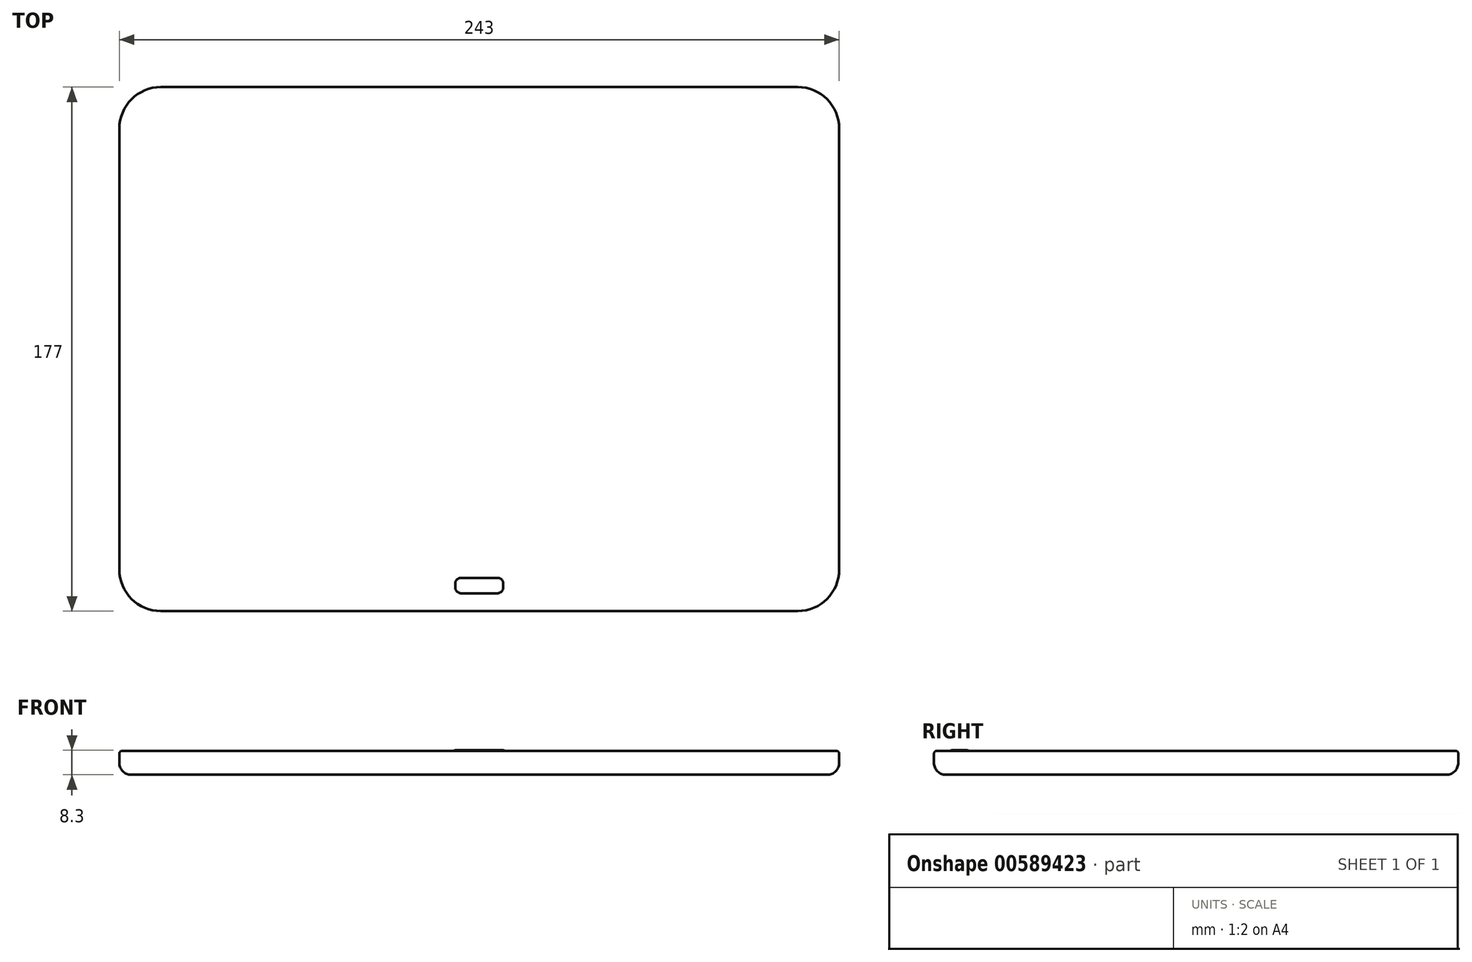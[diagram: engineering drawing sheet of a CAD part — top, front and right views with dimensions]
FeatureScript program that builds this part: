
annotation { "Feature Type Name" : "Feature", "Feature Type Description" : "" }
export const myFeature = defineFeature(function(context is Context, id is Id, definition is map)
    precondition{}
    {
        {
            var Q0;
            Q0=qCreatedBy(makeId("Top.planeOp"),FACE);
            var sketch = newSketch(context, id + "F0", { "sketchPlane" : qUnion([Q0])});
            skLineSegment(sketch, "E0.bottom", {"start": v(-121.5, 177) * mm, "end": v(121.5, 177) * mm});
            skLineSegment(sketch, "E0.top", {"start": v(-121.5, 0) * mm, "end": v(121.5, 0) * mm});
            skLineSegment(sketch, "E0.left", {"start": v(-121.5, 177) * mm, "end": v(-121.5, 0) * mm});
            skLineSegment(sketch, "E0.right", {"start": v(121.5, 177) * mm, "end": v(121.5, 0) * mm});
            skSolve(sketch);
        }
        {
            var Q0;
            Q0=makeQuery(id+"F0.imprint","IMPRINT",FACE,{"disambiguationData":[TD([[makeQuery(id+"F0.imprint","IMPRINT",EDGE,{"derivedFrom":sQuery(id+"F0.wireOp",EDGE,"E0.bottom")}),-1.0]])]});
            extrude(context, id + "F1", {"entities" : qUnion([Q0]), "depth" : 8.1 * mm, "offsetDistance" : 25 * mm});
        }
        {
            var Q0;
            Q0=makeQuery(id+"F1.opExtrude","SWEPT_EDGE",EDGE,{"disambiguationData":[OSD([sQuery(id+"F0.wireOp",EDGE,"E0.top"),sQuery(id+"F0.wireOp",EDGE,"E0.left")])]});
            var Q1;
            Q1=makeQuery(id+"F1.opExtrude","SWEPT_EDGE",EDGE,{"disambiguationData":[OSD([sQuery(id+"F0.wireOp",EDGE,"E0.top"),sQuery(id+"F0.wireOp",EDGE,"E0.right")])]});
            var Q2;
            Q2=makeQuery(id+"F1.opExtrude","SWEPT_EDGE",EDGE,{"disambiguationData":[OSD([sQuery(id+"F0.wireOp",EDGE,"E0.bottom"),sQuery(id+"F0.wireOp",EDGE,"E0.right")])]});
            var Q3;
            Q3=makeQuery(id+"F1.opExtrude","SWEPT_EDGE",EDGE,{"disambiguationData":[OSD([sQuery(id+"F0.wireOp",EDGE,"E0.bottom"),sQuery(id+"F0.wireOp",EDGE,"E0.left")])]});
            fillet(context, id + "F2", {"entities" : qUnion([Q0, Q1, Q2, Q3]), "radius" : 14 * mm, "tangentPropagation" : true, "allowEdgeOverflow" : false});
        }
        {
            var Q0;
            Q0=makeQuery(id+"F1.opExtrude","CAP_FACE",FACE,{"disambiguationData":[OSD([sQuery(id+"F0.wireOp",EDGE,"E0.bottom"),sQuery(id+"F0.wireOp",EDGE,"E0.top"),sQuery(id+"F0.wireOp",EDGE,"E0.left"),sQuery(id+"F0.wireOp",EDGE,"E0.right")])],"isStart":false});
            var sketch = newSketch(context, id + "F3", { "sketchPlane" : qUnion([Q0])});
            skLineSegment(sketch, "E1.bottom", {"start": v(-8.1, 11.2) * mm, "end": v(8.1, 11.2) * mm});
            skLineSegment(sketch, "E1.top", {"start": v(-8.1, 6) * mm, "end": v(8.1, 6) * mm});
            skLineSegment(sketch, "E1.left", {"start": v(-8.1, 11.2) * mm, "end": v(-8.1, 6) * mm});
            skLineSegment(sketch, "E1.right", {"start": v(8.1, 11.2) * mm, "end": v(8.1, 6) * mm});
            skPoint(sketch, "E2.0", {"position": v(0, 0) * mm});
            skLineSegment(sketch, "E3", {"start": v(0, 0) * mm, "end": v(0, 6) * mm, "construction": true});
            skSolve(sketch);
        }
        {
            var Q0;
            Q0=makeQuery(id+"F3.imprint","IMPRINT",FACE,{"disambiguationData":[TD([[makeQuery(id+"F3.imprint","IMPRINT",EDGE,{"derivedFrom":sQuery(id+"F3.wireOp",EDGE,"E1.bottom")}),-1.0]])]});
            extrude(context, id + "F4", {"entities" : qUnion([Q0]), "operationType" : NewBodyOperationType.ADD, "depth" : 0.2 * mm, "offsetDistance" : 25 * mm});
        }
        {
            var Q0;
            Q0=makeQuery(id+"F4.opExtrude","SWEPT_EDGE",EDGE,{"disambiguationData":[OSD([sQuery(id+"F3.wireOp",EDGE,"E1.top"),sQuery(id+"F3.wireOp",EDGE,"E1.right")])]});
            var Q1;
            Q1=makeQuery(id+"F4.opExtrude","SWEPT_EDGE",EDGE,{"disambiguationData":[OSD([sQuery(id+"F3.wireOp",EDGE,"E1.bottom"),sQuery(id+"F3.wireOp",EDGE,"E1.right")])]});
            var Q2;
            Q2=makeQuery(id+"F4.opExtrude","SWEPT_EDGE",EDGE,{"disambiguationData":[OSD([sQuery(id+"F3.wireOp",EDGE,"E1.top"),sQuery(id+"F3.wireOp",EDGE,"E1.left")])]});
            var Q3;
            Q3=makeQuery(id+"F4.opExtrude","SWEPT_EDGE",EDGE,{"disambiguationData":[OSD([sQuery(id+"F3.wireOp",EDGE,"E1.bottom"),sQuery(id+"F3.wireOp",EDGE,"E1.left")])]});
            fillet(context, id + "F5", {"entities" : qUnion([Q0, Q1, Q2, Q3]), "radius" : 2 * mm, "tangentPropagation" : true, "allowEdgeOverflow" : false});
        }
        {
            var Q0;
            Q0=makeQuery(id+"F1.opExtrude","CAP_EDGE",EDGE,{"disambiguationData":[OSD([sQuery(id+"F0.wireOp",EDGE,"E0.right")])],"isStart":true});
            fillet(context, id + "F6", {"entities" : qUnion([Q0]), "radius" : 4 * mm, "tangentPropagation" : true, "allowEdgeOverflow" : false});
        }
        {
            var Q0;
            Q0=makeQuery(id+"F1.opExtrude","CAP_FACE",FACE,{"disambiguationData":[OSD([sQuery(id+"F0.wireOp",EDGE,"E0.bottom"),sQuery(id+"F0.wireOp",EDGE,"E0.top"),sQuery(id+"F0.wireOp",EDGE,"E0.left"),sQuery(id+"F0.wireOp",EDGE,"E0.right")])],"isStart":false});
            fillet(context, id + "F7", {"entities" : qUnion([Q0]), "radius" : 1 * mm, "tangentPropagation" : true, "allowEdgeOverflow" : false});
        }
    });
